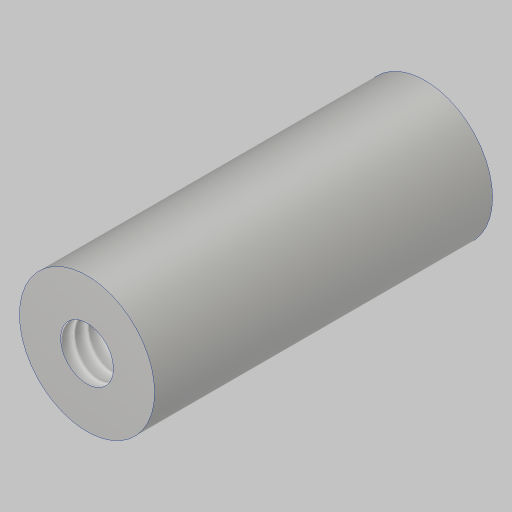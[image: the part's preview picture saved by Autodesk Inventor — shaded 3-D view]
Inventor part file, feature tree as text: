
AUTODESK INVENTOR PART (.ipt)
format: ipt  version: 2023.5 (Build 275446000, 446)  size: 114,176 bytes
history: native  units: in
note: dims shown in document units (in); Inventor stores cm internally (conversion verified against a paired STEP export)
features: sketch x2, extrude x1, hole x1
ambient origin geometry x8: Origin, YZ Plane, XZ Plane, XY Plane, X Axis, Y Axis, Z Axis, Center Point
bodies: Solid1 (feature_tree)
feature tree (4):
  extrude  "Extrusion1"  Depth=1.25in TaperAngle=0.0deg
  hole  "Hole1"  [1 undecoded]
  sketch  "Sketch1"  dims[d0=0.5in d1=1.25in d2=0.0in]
  sketch  "Sketch2"  dims[d3=0.196in d4=0.5in d5=0.507in d6=0.25in d7=0.5635in d8=1.0in d9=0.8108in]
note: 1 required parameter value undecoded (feature->parameter linkage not recoverable at this tier; creation-order binding heuristic only, values carry confidence <= 0.55)
